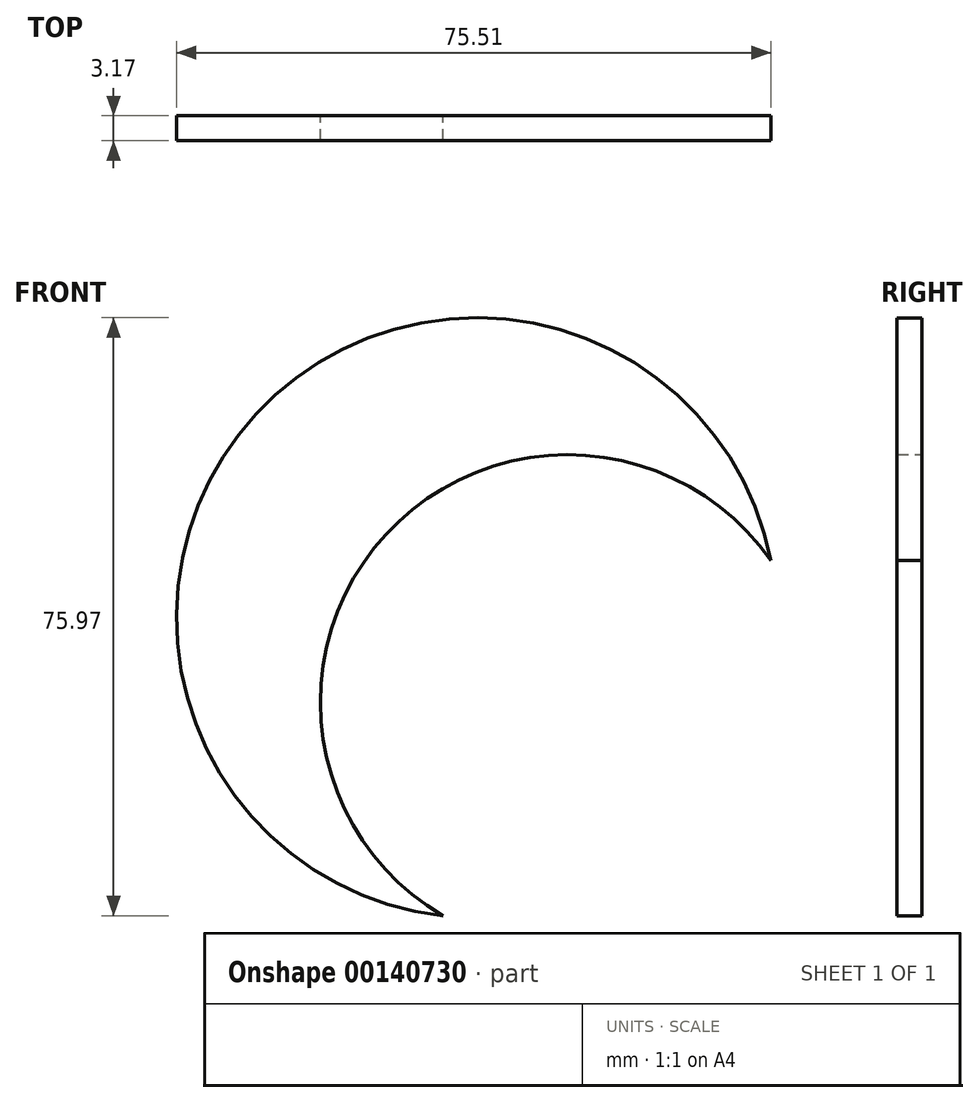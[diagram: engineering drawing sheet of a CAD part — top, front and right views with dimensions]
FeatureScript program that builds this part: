
annotation { "Feature Type Name" : "Feature", "Feature Type Description" : "" }
export const myFeature = defineFeature(function(context is Context, id is Id, definition is map)
    precondition{}
    {
        {
            var Q0;
            Q0=qCreatedBy(makeId("Front.planeOp"),FACE);
            var sketch = newSketch(context, id + "F0", { "sketchPlane" : qUnion([Q0])});
            skArc(sketch, "E0", {"start": v(-6.1, 31.24) * mm, "mid": v(-71.5, 49.83) * mm, "end": v(-47.74, -13.88) * mm});
            skArc(sketch, "E1", {"start": v(-6.1, 31.24) * mm, "mid": v(-54.98, 34.58) * mm, "end": v(-47.74, -13.88) * mm});
            skSolve(sketch);
        }
        {
            var Q0;
            {var subQ0=sQuery(id+"F0.wireOp",EDGE,"E1");var subQ1=sQuery(id+"F0.wireOp",EDGE,"E0");var subQ2=makeQuery(id+"F0.imprint","INTERSECT",VERTEX,{"disambiguationData":[OD(0.0)],"derivedFrom":[subQ1,subQ0]});Q0=makeQuery(id+"F0.imprint","IMPRINT",FACE,{"disambiguationData":[TD([[makeQuery(id+"F0.imprint","IMPRINT",EDGE,{"disambiguationData":[TD([[subQ2,1.0]])],"derivedFrom":subQ1}),1.0]])]});}
            extrude(context, id + "F1", {"entities" : qUnion([Q0]), "depth" : 3.17 * mm});
        }
    });
